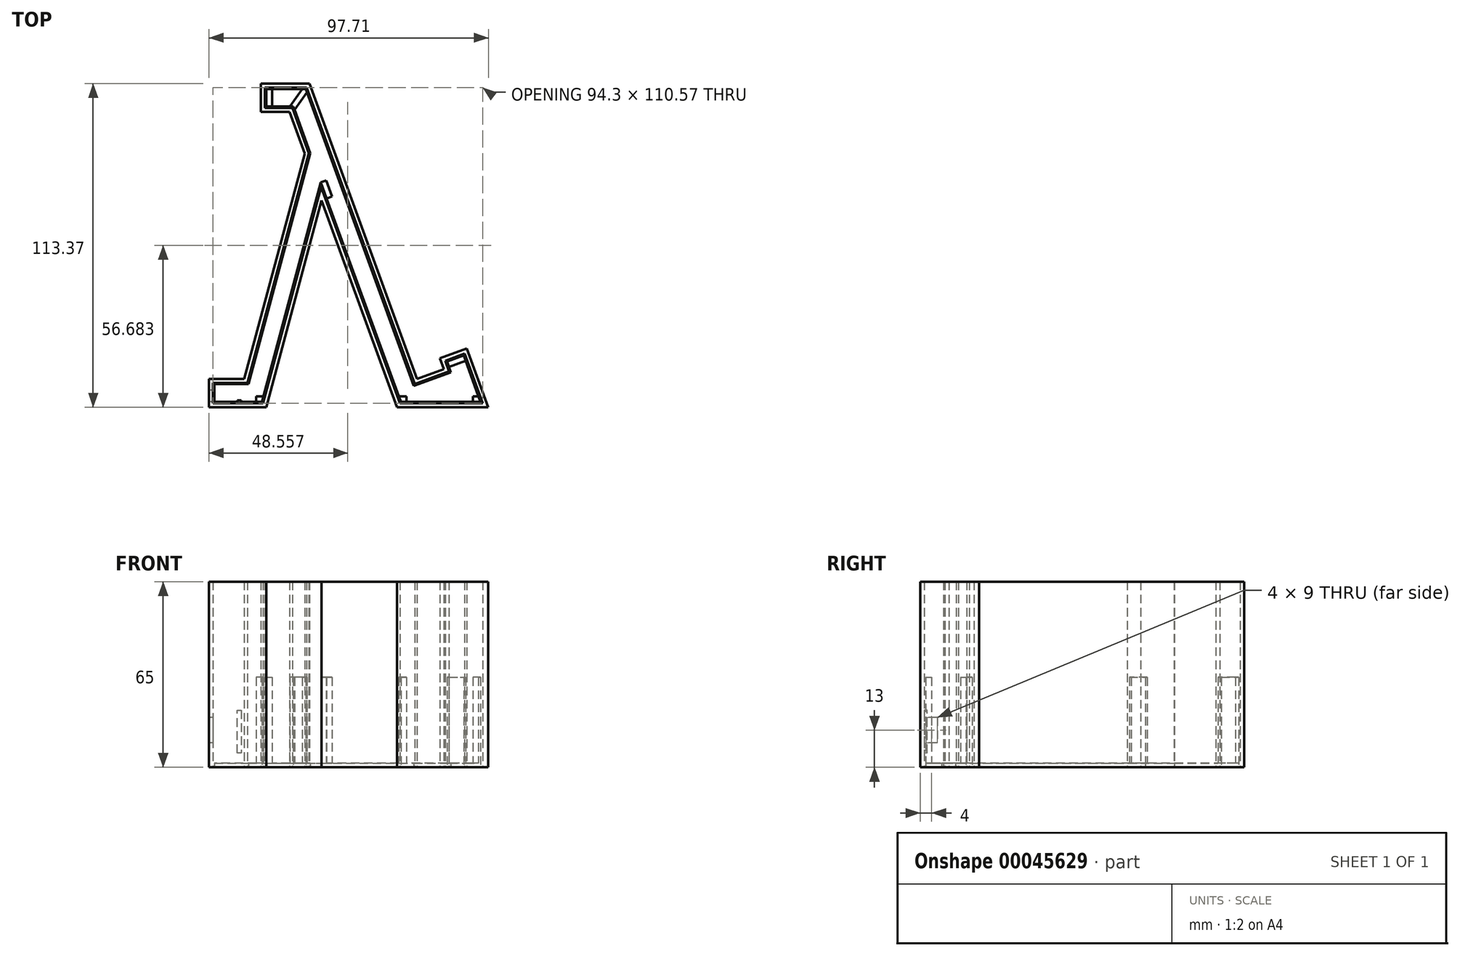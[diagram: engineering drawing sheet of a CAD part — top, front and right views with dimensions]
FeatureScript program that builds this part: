
annotation { "Feature Type Name" : "Feature", "Feature Type Description" : "" }
export const myFeature = defineFeature(function(context is Context, id is Id, definition is map)
    precondition{}
    {
        {
            var Q0;
            Q0=qCreatedBy(makeId("Top.planeOp"),FACE);
            var sketch = newSketch(context, id + "F0", { "sketchPlane" : qUnion([Q0])});
            skLineSegment(sketch, "E0", {"start": v(26.13, 0) * mm, "end": v(-0.23, 72.44) * mm});
            skLineSegment(sketch, "E1", {"start": v(-11.49, 103.37) * mm, "end": v(-21.49, 103.37) * mm});
            skLineSegment(sketch, "E2", {"start": v(-21.49, 103.37) * mm, "end": v(-21.49, 113.37) * mm});
            skLineSegment(sketch, "E3", {"start": v(-21.49, 113.37) * mm, "end": v(-4.49, 113.37) * mm});
            skLineSegment(sketch, "E4", {"start": v(-4.49, 113.37) * mm, "end": v(33.14, 10) * mm});
            skLineSegment(sketch, "E5", {"start": v(33.14, 10) * mm, "end": v(42.53, 13.42) * mm});
            skLineSegment(sketch, "E6", {"start": v(42.53, 13.42) * mm, "end": v(41.16, 17.18) * mm});
            skLineSegment(sketch, "E7", {"start": v(41.16, 17.18) * mm, "end": v(50.56, 20.6) * mm});
            skLineSegment(sketch, "E8", {"start": v(50.56, 20.6) * mm, "end": v(58.06, 0) * mm});
            skLineSegment(sketch, "E9", {"start": v(58.06, 0) * mm, "end": v(26.13, 0) * mm});
            skLineSegment(sketch, "E10", {"start": v(-19.65, 0) * mm, "end": v(-0.23, 72.44) * mm});
            skLineSegment(sketch, "E11", {"start": v(-19.65, 0) * mm, "end": v(-39.65, 0) * mm});
            skLineSegment(sketch, "E12", {"start": v(-39.65, 0) * mm, "end": v(-39.65, 10) * mm});
            skLineSegment(sketch, "E13", {"start": v(-39.65, 10) * mm, "end": v(-27.32, 10) * mm});
            skLineSegment(sketch, "E14", {"start": v(-27.32, 10) * mm, "end": v(-6.2, 88.83) * mm});
            skLineSegment(sketch, "E15", {"start": v(-0.23, 72.44) * mm, "end": v(-0.23, 0) * mm, "construction": true});
            skLineSegment(sketch, "E16.trimOffspring", {"start": v(-6.2, 88.83) * mm, "end": v(-11.49, 103.37) * mm});
            skLineSegment(sketch, "E17.0", {"start": v(-20.09, 104.77) * mm, "end": v(-20.09, 111.97) * mm});
            skLineSegment(sketch, "E17.1", {"start": v(-10.5, 104.77) * mm, "end": v(-20.09, 104.77) * mm});
            skLineSegment(sketch, "E17.2", {"start": v(-4.73, 88.9) * mm, "end": v(-10.5, 104.77) * mm});
            skLineSegment(sketch, "E17.3", {"start": v(-26.24, 8.6) * mm, "end": v(-4.73, 88.9) * mm});
            skLineSegment(sketch, "E17.4", {"start": v(-38.25, 8.6) * mm, "end": v(-26.24, 8.6) * mm});
            skLineSegment(sketch, "E17.5", {"start": v(42.96, 16.34) * mm, "end": v(49.72, 18.8) * mm});
            skLineSegment(sketch, "E17.6", {"start": v(44.33, 12.58) * mm, "end": v(42.96, 16.34) * mm});
            skLineSegment(sketch, "E17.7", {"start": v(32.3, 8.2) * mm, "end": v(44.33, 12.58) * mm});
            skLineSegment(sketch, "E17.8", {"start": v(-5.47, 111.97) * mm, "end": v(32.3, 8.2) * mm});
            skLineSegment(sketch, "E17.9", {"start": v(49.72, 18.8) * mm, "end": v(56.06, 1.4) * mm});
            skLineSegment(sketch, "E17.10", {"start": v(56.06, 1.4) * mm, "end": v(27.11, 1.4) * mm});
            skLineSegment(sketch, "E17.11", {"start": v(27.11, 1.4) * mm, "end": v(-0.44, 77.1) * mm});
            skLineSegment(sketch, "E17.12", {"start": v(-20.72, 1.4) * mm, "end": v(-0.44, 77.1) * mm});
            skLineSegment(sketch, "E17.13", {"start": v(-20.72, 1.4) * mm, "end": v(-38.25, 1.4) * mm});
            skLineSegment(sketch, "E17.14", {"start": v(-20.09, 111.97) * mm, "end": v(-5.47, 111.97) * mm});
            skLineSegment(sketch, "E17.15", {"start": v(-38.25, 1.4) * mm, "end": v(-38.25, 8.6) * mm});
            skLineSegment(sketch, "E18.0", {"start": v(-10.16, 105.27) * mm, "end": v(-19.59, 105.27) * mm});
            skLineSegment(sketch, "E18.1", {"start": v(-4.2, 88.91) * mm, "end": v(-10.16, 105.27) * mm});
            skLineSegment(sketch, "E18.2", {"start": v(-25.86, 8.1) * mm, "end": v(-4.2, 88.91) * mm});
            skLineSegment(sketch, "E18.3", {"start": v(-37.75, 8.1) * mm, "end": v(-25.86, 8.1) * mm});
            skLineSegment(sketch, "E18.4", {"start": v(-37.75, 1.9) * mm, "end": v(-37.75, 8.1) * mm});
            skLineSegment(sketch, "E18.5", {"start": v(44.97, 12.28) * mm, "end": v(43.6, 16.04) * mm});
            skLineSegment(sketch, "E18.6", {"start": v(32, 7.56) * mm, "end": v(44.97, 12.28) * mm});
            skLineSegment(sketch, "E18.7", {"start": v(-5.82, 111.47) * mm, "end": v(32, 7.56) * mm});
            skLineSegment(sketch, "E18.8", {"start": v(-19.59, 111.47) * mm, "end": v(-5.82, 111.47) * mm});
            skLineSegment(sketch, "E18.9", {"start": v(43.6, 16.04) * mm, "end": v(49.43, 18.16) * mm});
            skLineSegment(sketch, "E18.10", {"start": v(49.43, 18.16) * mm, "end": v(55.35, 1.9) * mm});
            skLineSegment(sketch, "E18.11", {"start": v(55.35, 1.9) * mm, "end": v(27.46, 1.9) * mm});
            skLineSegment(sketch, "E18.12", {"start": v(27.46, 1.9) * mm, "end": v(-0.5, 78.76) * mm});
            skLineSegment(sketch, "E18.13", {"start": v(-21.1, 1.9) * mm, "end": v(-0.5, 78.76) * mm});
            skLineSegment(sketch, "E18.14", {"start": v(-19.59, 105.27) * mm, "end": v(-19.59, 111.47) * mm});
            skLineSegment(sketch, "E18.15", {"start": v(-21.1, 1.9) * mm, "end": v(-37.75, 1.9) * mm});
            skSolve(sketch);
        }
        {
            var Q0;
            Q0=makeQuery(id+"F0.imprint","IMPRINT",FACE,{"disambiguationData":[TD([[makeQuery(id+"F0.imprint","IMPRINT",EDGE,{"derivedFrom":sQuery(id+"F0.wireOp",EDGE,"E0")}),-1.0]])]});
            extrude(context, id + "F1", {"entities" : qUnion([Q0]), "depth" : 65 * mm});
        }
        {
            var Q0;
            Q0=makeQuery(id+"F0.imprint","IMPRINT",FACE,{"disambiguationData":[TD([[makeQuery(id+"F0.imprint","IMPRINT",EDGE,{"derivedFrom":sQuery(id+"F0.wireOp",EDGE,"E18.0")}),-1.0]])]});
            extrude(context, id + "F2", {"entities" : qUnion([Q0]), "depth" : 1.5 * mm});
        }
        {
            var Q0;
            Q0=makeQuery(id+"F2.opExtrude","CAP_FACE",FACE,{"disambiguationData":[OSD([sQuery(id+"F0.wireOp",EDGE,"E18.0"),sQuery(id+"F0.wireOp",EDGE,"E18.1"),sQuery(id+"F0.wireOp",EDGE,"E18.2"),sQuery(id+"F0.wireOp",EDGE,"E18.3"),sQuery(id+"F0.wireOp",EDGE,"E18.4"),sQuery(id+"F0.wireOp",EDGE,"E18.5"),sQuery(id+"F0.wireOp",EDGE,"E18.6"),sQuery(id+"F0.wireOp",EDGE,"E18.7"),sQuery(id+"F0.wireOp",EDGE,"E18.8"),sQuery(id+"F0.wireOp",EDGE,"E18.9"),sQuery(id+"F0.wireOp",EDGE,"E18.10"),sQuery(id+"F0.wireOp",EDGE,"E18.11"),sQuery(id+"F0.wireOp",EDGE,"E18.12"),sQuery(id+"F0.wireOp",EDGE,"E18.13"),sQuery(id+"F0.wireOp",EDGE,"E18.14"),sQuery(id+"F0.wireOp",EDGE,"E18.15")])],"isStart":false});
            var sketch = newSketch(context, id + "F3", { "sketchPlane" : qUnion([Q0])});
            skLineSegment(sketch, "E19", {"start": v(-17.59, 111.47) * mm, "end": v(-17.59, 105.27) * mm});
            skLineSegment(sketch, "E20", {"start": v(-10.16, 105.27) * mm, "end": v(-5.82, 111.47) * mm, "construction": true});
            skLineSegment(sketch, "E21", {"start": v(-7.04, 111.47) * mm, "end": v(-11.38, 105.27) * mm});
            skLineSegment(sketch, "E22", {"start": v(-5.4, 110.32) * mm, "end": v(-9.74, 104.12) * mm});
            skLineSegment(sketch, "E23", {"start": v(-20.57, 3.9) * mm, "end": v(-23.1, 3.9) * mm});
            skLineSegment(sketch, "E24", {"start": v(-23.1, 3.9) * mm, "end": v(-23.1, 1.9) * mm});
            skLineSegment(sketch, "E25", {"start": v(44.28, 14.16) * mm, "end": v(50.1, 16.28) * mm});
            skLineSegment(sketch, "E26", {"start": v(54.62, 3.9) * mm, "end": v(52.62, 3.9) * mm});
            skLineSegment(sketch, "E27", {"start": v(52.62, 3.9) * mm, "end": v(52.62, 1.9) * mm});
            skLineSegment(sketch, "E28", {"start": v(26.74, 3.9) * mm, "end": v(29.46, 3.9) * mm});
            skLineSegment(sketch, "E29", {"start": v(29.46, 3.9) * mm, "end": v(29.46, 1.9) * mm});
            skLineSegment(sketch, "E30", {"start": v(-0.5, 78.76) * mm, "end": v(1.37, 79.44) * mm});
            skLineSegment(sketch, "E31", {"start": v(1.37, 79.44) * mm, "end": v(3.42, 73.8) * mm});
            skLineSegment(sketch, "E32", {"start": v(3.42, 73.8) * mm, "end": v(1.54, 73.12) * mm});
            skSolve(sketch);
        }
        {
            var Q0;
            {var subQ1=sQuery(id+"F3.wireOp",EDGE,"E19");Q0=makeQuery(id+"F3.imprint","IMPRINT",FACE,{"disambiguationData":[TD([[makeQuery(id+"F3.imprint","IMPRINT",EDGE,{"derivedFrom":subQ1}),-1.0]])]});}
            var Q1;
            {var subQ1=sQuery(id+"F3.wireOp",EDGE,"E21");Q1=makeQuery(id+"F3.imprint","IMPRINT",FACE,{"disambiguationData":[TD([[makeQuery(id+"F3.imprint","IMPRINT",EDGE,{"derivedFrom":subQ1}),1.0]])]});}
            var Q2;
            {var subQ2=sQuery(id+"F3.wireOp",EDGE,"E30");Q2=makeQuery(id+"F3.imprint","IMPRINT",FACE,{"disambiguationData":[TD([[makeQuery(id+"F3.imprint","IMPRINT",EDGE,{"derivedFrom":subQ2}),-1.0]])]});}
            var Q3;
            {var subQ1=sQuery(id+"F3.wireOp",EDGE,"E25");Q3=makeQuery(id+"F3.imprint","IMPRINT",FACE,{"disambiguationData":[TD([[makeQuery(id+"F3.imprint","IMPRINT",EDGE,{"derivedFrom":subQ1}),1.0]])]});}
            var Q4;
            {var subQ4=sQuery(id+"F3.wireOp",EDGE,"E26");Q4=makeQuery(id+"F3.imprint","IMPRINT",FACE,{"disambiguationData":[TD([[makeQuery(id+"F3.imprint","IMPRINT",EDGE,{"derivedFrom":subQ4}),1.0]])]});}
            var Q5;
            {var subQ1=sQuery(id+"F3.wireOp",EDGE,"E28");Q5=makeQuery(id+"F3.imprint","IMPRINT",FACE,{"disambiguationData":[TD([[makeQuery(id+"F3.imprint","IMPRINT",EDGE,{"derivedFrom":subQ1}),-1.0]])]});}
            var Q6;
            {var subQ4=sQuery(id+"F3.wireOp",EDGE,"E23");Q6=makeQuery(id+"F3.imprint","IMPRINT",FACE,{"disambiguationData":[TD([[makeQuery(id+"F3.imprint","IMPRINT",EDGE,{"derivedFrom":subQ4}),1.0]])]});}
            extrude(context, id + "F4", {"entities" : qUnion([Q0, Q1, Q2, Q3, Q4, Q5, Q6]), "operationType" : NewBodyOperationType.ADD, "depth" : 30 * mm});
        }
        {
            var Q0;
            Q0=makeQuery(id+"F1.opExtrude","SWEPT_FACE",FACE,{"disambiguationData":[OSD([sQuery(id+"F0.wireOp",EDGE,"E17.13")])]});
            var sketch = newSketch(context, id + "F5", { "sketchPlane" : qUnion([Q0])});
            skLineSegment(sketch, "E33", {"start": v(29.75, 0) * mm, "end": v(29.75, 20) * mm});
            skLineSegment(sketch, "E34", {"start": v(29.75, 20) * mm, "end": v(28.35, 20) * mm});
            skLineSegment(sketch, "E35", {"start": v(28.35, 20) * mm, "end": v(28.35, 0) * mm});
            skLineSegment(sketch, "E36", {"start": v(28.35, 5) * mm, "end": v(29.75, 5) * mm});
            skSolve(sketch);
        }
        {
            var Q0;
            {var subQ0=sQuery(id+"F5.wireOp",EDGE,"E34");Q0=makeQuery(id+"F5.imprint","IMPRINT",FACE,{"disambiguationData":[TD([[makeQuery(id+"F5.imprint","IMPRINT",EDGE,{"derivedFrom":subQ0}),1.0]])]});}
            extrude(context, id + "F6", {"entities" : qUnion([Q0]), "operationType" : NewBodyOperationType.ADD, "depth" : 1 * mm});
        }
        {
            var Q0;
            Q0=makeQuery(id+"F1.opExtrude","SWEPT_FACE",FACE,{"disambiguationData":[OSD([sQuery(id+"F0.wireOp",EDGE,"E12")])]});
            var sketch = newSketch(context, id + "F7", { "sketchPlane" : qUnion([Q0])});
            skLineSegment(sketch, "E37", {"start": v(-4, 0) * mm, "end": v(-4, 13) * mm, "construction": true});
            skLineSegment(sketch, "E38.rect.bottom", {"start": v(-2, 8.5) * mm, "end": v(-6, 8.5) * mm});
            skLineSegment(sketch, "E38.rect.top", {"start": v(-2, 17.5) * mm, "end": v(-6, 17.5) * mm});
            skLineSegment(sketch, "E38.rect.left", {"start": v(-2, 8.5) * mm, "end": v(-2, 17.5) * mm});
            skLineSegment(sketch, "E38.rect.right", {"start": v(-6, 8.5) * mm, "end": v(-6, 17.5) * mm});
            skPoint(sketch, "E38.rect.middle", {"position": v(-4, 13) * mm});
            skSolve(sketch);
        }
        {
            var Q0;
            Q0=makeQuery(id+"F7.imprint","IMPRINT",FACE,{"disambiguationData":[TD([[makeQuery(id+"F7.imprint","IMPRINT",EDGE,{"derivedFrom":sQuery(id+"F7.wireOp",EDGE,"E38.rect.bottom")}),-1.0]])]});
            extrude(context, id + "F8", {"entities" : qUnion([Q0]), "operationType" : NewBodyOperationType.REMOVE, "endBound" : BoundingType.UP_TO_NEXT, "oppositeDirection" : true, "depth" : 25 * mm});
        }
    });
